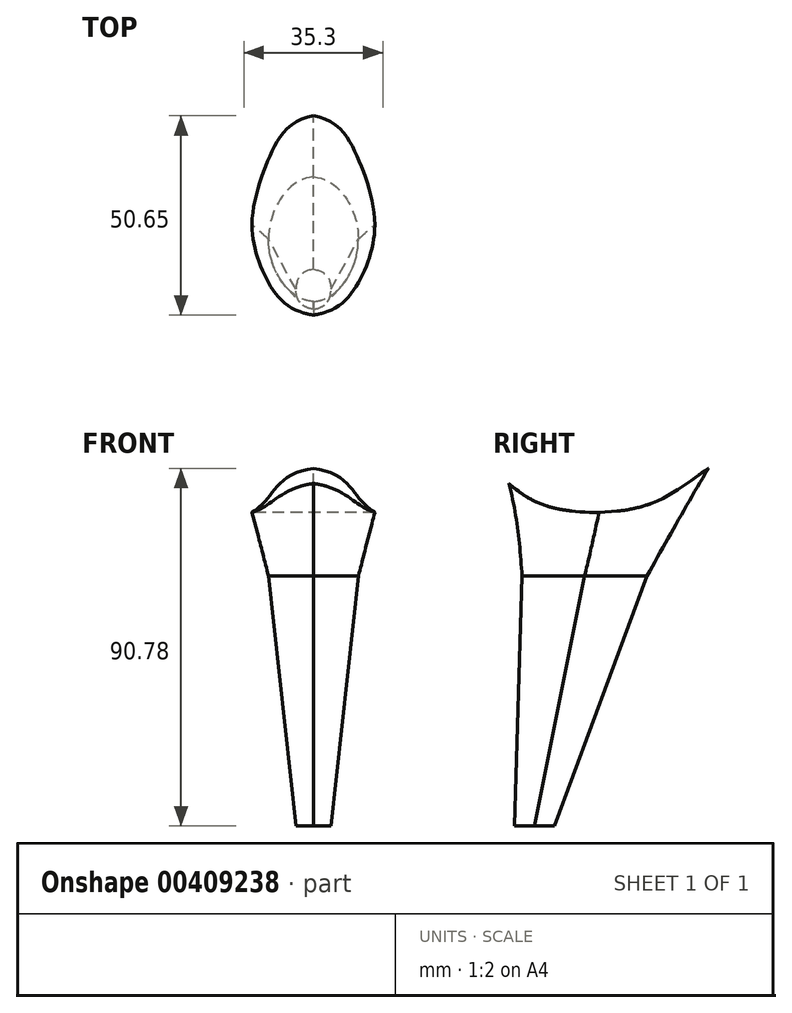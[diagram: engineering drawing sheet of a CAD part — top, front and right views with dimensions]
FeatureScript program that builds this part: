
annotation { "Feature Type Name" : "Feature", "Feature Type Description" : "" }
export const myFeature = defineFeature(function(context is Context, id is Id, definition is map)
    precondition{}
    {
        {
            var Q0;
            Q0=qCreatedBy(makeId("Top.planeOp"),FACE);
            var sketch = newSketch(context, id + "F0", { "sketchPlane" : qUnion([Q0])});
            skCircle(sketch, "E0", {"center": v(0, 0) * mm, "radius": 4.45 * mm, "construction": true});
            skFitSpline(sketch, "E1", {"points": [v(0, 5.08) * mm, v(-3.16, 3.63) * mm, v(-4.45, 0) * mm], "startDerivative": vector(-10.05, -1.39) * mm, "endDerivative": vector(-0.35, -12.15) * mm});
            skCircle(sketch, "E2", {"center": v(0, 0) * mm, "radius": 5.08 * mm, "construction": true});
            skFitSpline(sketch, "E3.MirrorCS", {"points": [v(0, 5.08) * mm, v(3.16, 3.63) * mm, v(4.45, 0) * mm], "startDerivative": vector(10.05, -1.39) * mm, "endDerivative": vector(0.35, -12.15) * mm});
            skFitSpline(sketch, "E4.MirrorCS", {"points": [v(0, 5.08) * mm, v(3.16, 3.63) * mm, v(4.45, 0) * mm], "startDerivative": vector(10.05, -1.39) * mm, "endDerivative": vector(0.35, -12.15) * mm});
            skFitSpline(sketch, "E5.MirrorCS", {"points": [v(0, -5.08) * mm, v(-3.16, -3.63) * mm, v(-4.45, 0) * mm], "startDerivative": vector(-10.05, 1.39) * mm, "endDerivative": vector(-0.35, 12.15) * mm});
            skFitSpline(sketch, "E6.MirrorCS", {"points": [v(0, -5.08) * mm, v(3.16, -3.63) * mm, v(4.45, 0) * mm], "startDerivative": vector(10.05, 1.39) * mm, "endDerivative": vector(0.35, 12.15) * mm});
            skSolve(sketch);
        }
        {
            var Q0;
            Q0=qCreatedBy(makeId("Top.planeOp"),FACE);
            cPlane(context, id + "F1", {"entities" : qUnion([Q0]), "cplaneType" : CPlaneType.OFFSET, "offset" : 63.5 * mm, "width" : 152.4 * mm, "height" : 152.4 * mm});
        }
        {
            var Q0;
            Q0=qCreatedBy(id+"F1.planeOp",FACE);
            var sketch = newSketch(context, id + "F2", { "sketchPlane" : qUnion([Q0])});
            skCircle(sketch, "E7", {"center": v(0, 12.7) * mm, "radius": 11.43 * mm, "construction": true});
            skCircle(sketch, "E8", {"center": v(0, 12.7) * mm, "radius": 15.88 * mm, "construction": true});
            skFitSpline(sketch, "E9", {"points": [v(0, 28.57) * mm, v(-7.97, 23.55) * mm, v(-11.43, 12.7) * mm], "startDerivative": vector(-23.5, -2.8) * mm, "endDerivative": vector(-0.5, -26.09) * mm});
            skFitSpline(sketch, "E10.MirrorCS", {"points": [v(0, 28.57) * mm, v(7.97, 23.55) * mm, v(11.43, 12.7) * mm], "startDerivative": vector(23.5, -2.8) * mm, "endDerivative": vector(0.5, -26.09) * mm});
            skLineSegment(sketch, "E11", {"start": v(-11.43, 12.7) * mm, "end": v(11.43, 12.7) * mm, "construction": true});
            skFitSpline(sketch, "E12.MirrorCS", {"points": [v(0, -3.17) * mm, v(-7.97, 1.85) * mm, v(-11.43, 12.7) * mm], "startDerivative": vector(-23.5, 2.8) * mm, "endDerivative": vector(-0.5, 26.09) * mm});
            skFitSpline(sketch, "E13.MirrorCS", {"points": [v(0, -3.17) * mm, v(7.97, 1.85) * mm, v(11.43, 12.7) * mm], "startDerivative": vector(23.5, 2.8) * mm, "endDerivative": vector(0.5, 26.09) * mm});
            skPoint(sketch, "E14.0", {"position": v(0, 0) * mm});
            skSolve(sketch);
        }
        {
            var Q0;
            Q0=makeQuery(id+"F0.imprint","IMPRINT",FACE,{"disambiguationData":[TD([[makeQuery(id+"F0.imprint","IMPRINT",EDGE,{"derivedFrom":sQuery(id+"F0.wireOp",EDGE,"E1")}),1.0]])]});
            var Q1;
            Q1=makeQuery(id+"F2.imprint","IMPRINT",FACE,{"disambiguationData":[TD([[makeQuery(id+"F2.imprint","IMPRINT",EDGE,{"derivedFrom":sQuery(id+"F2.wireOp",EDGE,"E9")}),1.0]])]});
            loft(context, id + "F3", {"sheetProfilesArray" : [{ "sheetProfileEntities" : qUnion([Q0]) }, { "sheetProfileEntities" : qUnion([Q1]) }]});
        }
        {
            var Q0;
            Q0=qCreatedBy(id+"F1.planeOp",FACE);
            cPlane(context, id + "F4", {"entities" : qUnion([Q0]), "cplaneType" : CPlaneType.OFFSET, "offset" : 38.1 * mm, "width" : 152.4 * mm, "height" : 152.4 * mm});
        }
        {
            var Q0;
            Q0=qCreatedBy(id+"F4.planeOp",FACE);
            var sketch = newSketch(context, id + "F5", { "sketchPlane" : qUnion([Q0])});
            skPoint(sketch, "E15.0", {"position": v(0, 0) * mm});
            skCircle(sketch, "E16", {"center": v(0, 19.05) * mm, "radius": 22.23 * mm, "construction": true});
            skCircle(sketch, "E17", {"center": v(0, 19.05) * mm, "radius": 31.75 * mm, "construction": true});
            skFitSpline(sketch, "E18", {"points": [v(0, 50.8) * mm, v(-14.15, 42.4) * mm, v(-22.22, 19.05) * mm], "startDerivative": vector(-46.14, -5.08) * mm, "endDerivative": vector(-0.3, -42.83) * mm});
            skLineSegment(sketch, "E19", {"start": v(-22.22, 19.05) * mm, "end": v(22.22, 19.05) * mm, "construction": true});
            skFitSpline(sketch, "E20.MirrorCS", {"points": [v(0, 50.8) * mm, v(14.15, 42.4) * mm, v(22.22, 19.05) * mm], "startDerivative": vector(46.14, -5.08) * mm, "endDerivative": vector(0.3, -42.83) * mm});
            skLineSegment(sketch, "E21.MirrorCS", {"start": v(22.22, 19.05) * mm, "end": v(-22.22, 19.05) * mm, "construction": true});
            skFitSpline(sketch, "E22.MirrorCS", {"points": [v(0, -12.7) * mm, v(-14.15, -4.3) * mm, v(-22.22, 19.05) * mm], "startDerivative": vector(-46.14, 5.08) * mm, "endDerivative": vector(-0.3, 42.83) * mm});
            skFitSpline(sketch, "E23.MirrorCS", {"points": [v(0, -12.7) * mm, v(14.15, -4.3) * mm, v(22.22, 19.05) * mm], "startDerivative": vector(46.14, 5.08) * mm, "endDerivative": vector(0.3, 42.83) * mm});
            skSolve(sketch);
        }
        {
            var Q0;
            Q0=qCreatedBy(id+"F4.planeOp",FACE);
            cPlane(context, id + "F6", {"entities" : qUnion([Q0]), "cplaneType" : CPlaneType.OFFSET, "offset" : 50.8 * mm, "width" : 152.4 * mm, "height" : 152.4 * mm});
        }
        {
            var Q0;
            Q0=qCreatedBy(id+"F6.planeOp",FACE);
            var sketch = newSketch(context, id + "F7", { "sketchPlane" : qUnion([Q0])});
            skPoint(sketch, "E24.0", {"position": v(0, 0) * mm});
            skCircle(sketch, "E25", {"center": v(0, 8.9) * mm, "radius": 44.45 * mm, "construction": true});
            skCircle(sketch, "E26", {"center": v(0, 8.9) * mm, "radius": 79.38 * mm, "construction": true});
            skFitSpline(sketch, "E27", {"points": [v(0, 88.26) * mm, v(-27.3, 62.72) * mm, v(-44.45, 8.9) * mm], "startDerivative": vector(-70.11, -4.65) * mm, "endDerivative": vector(4.08, -70.7) * mm});
            skLineSegment(sketch, "E28", {"start": v(-44.45, 8.9) * mm, "end": v(44.45, 8.9) * mm, "construction": true});
            skFitSpline(sketch, "E29.MirrorCS", {"points": [v(0, 88.26) * mm, v(27.3, 62.72) * mm, v(44.45, 8.9) * mm], "startDerivative": vector(70.11, -4.65) * mm, "endDerivative": vector(-4.08, -70.7) * mm});
            skFitSpline(sketch, "E30.MirrorCS", {"points": [v(0, -70.48) * mm, v(27.3, -44.94) * mm, v(44.45, 8.9) * mm], "startDerivative": vector(70.11, 4.65) * mm, "endDerivative": vector(-4.08, 70.7) * mm});
            skFitSpline(sketch, "E31.MirrorCS", {"points": [v(0, -70.48) * mm, v(-27.3, -44.94) * mm, v(-44.45, 8.9) * mm], "startDerivative": vector(-70.11, 4.65) * mm, "endDerivative": vector(4.08, 70.7) * mm});
            skSolve(sketch);
        }
        {
            var Q1;
            Q1=makeQuery(id+"F3.opLoft","CAP_FACE",FACE,{"disambiguationData":[OSD([makeQuery(id+"F2.imprint","IMPRINT",FACE,{"disambiguationData":[TD([[makeQuery(id+"F2.imprint","IMPRINT",EDGE,{"derivedFrom":sQuery(id+"F2.wireOp",EDGE,"E9")}),1.0]])]})])],"isStart":true});
            var Q2;
            Q2=makeQuery(id+"F5.imprint","IMPRINT",FACE,{"disambiguationData":[TD([[makeQuery(id+"F5.imprint","IMPRINT",EDGE,{"derivedFrom":sQuery(id+"F5.wireOp",EDGE,"E18")}),1.0]])]});
            var Q3;
            Q3=makeQuery(id+"F7.imprint","IMPRINT",FACE,{"disambiguationData":[TD([[makeQuery(id+"F7.imprint","IMPRINT",EDGE,{"derivedFrom":sQuery(id+"F7.wireOp",EDGE,"E27")}),1.0]])]});
            loft(context, id + "F8", {"sheetProfilesArray" : [{ "sheetProfileEntities" : qUnion([Q1]) }, { "sheetProfileEntities" : qUnion([Q2]) }, { "sheetProfileEntities" : qUnion([Q3]) }]});
        }
        {
            var Q0;
            Q0=qCreatedBy(makeId("Right.planeOp"),FACE);
            var sketch = newSketch(context, id + "F9", { "sketchPlane" : qUnion([Q0])});
            skFitSpline(sketch, "E32.0", {"points": [v(88.26, 152.4) * mm, v(77.06, 142.5) * mm, v(62.52, 131.17) * mm, v(37.92, 111.87) * mm, v(0.7, 109.17) * mm, v(-18.8, 117.07) * mm, v(-33.09, 124.93) * mm], "construction": true});
            skFitSpline(sketch, "E33.0", {"points": [v(-12.7, 101.6) * mm, v(-22.27, 119.4) * mm, v(-46.38, 135.9) * mm, v(-70.48, 152.4) * mm], "construction": true});
            skFitSpline(sketch, "E34.0", {"points": [v(50.8, 101.6) * mm, v(61.34, 119.4) * mm, v(74.8, 135.9) * mm, v(88.26, 152.4) * mm], "construction": true});
            skLineSegment(sketch, "E35", {"start": v(156.16, 101.92) * mm, "end": v(156.16, 185.2) * mm});
            skLineSegment(sketch, "E36", {"start": v(156.16, 185.2) * mm, "end": v(-81.97, 185.2) * mm});
            skLineSegment(sketch, "E37", {"start": v(-81.97, 185.2) * mm, "end": v(-81.97, 101.9) * mm});
            skFitSpline(sketch, "E38.0", {"points": [v(-6.74, 63.5) * mm, v(-6.42, 76.4) * mm, v(-6.1, 89.31) * mm, v(-12.7, 101.6) * mm]});
            skFitSpline(sketch, "E39.0", {"points": [v(31.75, 63.5) * mm, v(37.64, 76.4) * mm, v(43.52, 89.31) * mm, v(50.8, 101.6) * mm]});
            skFitSpline(sketch, "E40.0.0", {"points": [v(31.75, 63.5) * mm, v(37.64, 76.4) * mm, v(43.52, 89.31) * mm, v(50.8, 101.6) * mm], "construction": true});
            skFitSpline(sketch, "E40.0.1", {"points": [v(50.8, 101.6) * mm, v(61.34, 119.4) * mm, v(74.8, 135.9) * mm, v(88.26, 152.4) * mm], "construction": true});
            skFitSpline(sketch, "E40.0.2", {"points": [v(88.26, 152.4) * mm, v(61.8, 152.4) * mm, v(35.35, 152.4) * mm, v(8.9, 152.4) * mm], "construction": true});
            skFitSpline(sketch, "E40.0.3", {"points": [v(8.89, 152.4) * mm, v(14.21, 135.9) * mm, v(19.54, 119.4) * mm, v(19.05, 101.6) * mm], "construction": true});
            skFitSpline(sketch, "E40.0.4", {"points": [v(19.05, 101.6) * mm, v(18.71, 89.31) * mm, v(15.6, 76.4) * mm, v(12.5, 63.5) * mm], "construction": true});
            skFitSpline(sketch, "E40.0.5", {"points": [v(12.5, 63.5) * mm, v(18.92, 63.5) * mm, v(25.33, 63.5) * mm, v(31.75, 63.5) * mm], "construction": true});
            skFitSpline(sketch, "E41.0.0", {"points": [v(12.5, 63.5) * mm, v(15.6, 76.4) * mm, v(18.71, 89.31) * mm, v(19.05, 101.6) * mm], "construction": true});
            skFitSpline(sketch, "E41.0.1", {"points": [v(19.05, 101.6) * mm, v(19.54, 119.4) * mm, v(14.21, 135.9) * mm, v(8.9, 152.4) * mm], "construction": true});
            skFitSpline(sketch, "E41.0.2", {"points": [v(8.9, 152.4) * mm, v(-17.57, 152.4) * mm, v(-44.03, 152.4) * mm, v(-70.48, 152.4) * mm], "construction": true});
            skFitSpline(sketch, "E41.0.3", {"points": [v(-70.48, 152.4) * mm, v(-46.38, 135.9) * mm, v(-22.27, 119.4) * mm, v(-12.7, 101.6) * mm], "construction": true});
            skFitSpline(sketch, "E41.0.4", {"points": [v(-12.7, 101.6) * mm, v(-6.1, 89.31) * mm, v(-6.42, 76.4) * mm, v(-6.74, 63.5) * mm], "construction": true});
            skFitSpline(sketch, "E41.0.5", {"points": [v(-6.74, 63.5) * mm, v(-0.33, 63.5) * mm, v(6.09, 63.5) * mm, v(12.5, 63.5) * mm], "construction": true});
            skFitSpline(sketch, "E42.0.0", {"points": [v(31.75, 63.5) * mm, v(37.64, 76.4) * mm, v(43.52, 89.31) * mm, v(50.8, 101.6) * mm], "construction": true});
            skFitSpline(sketch, "E42.0.1", {"points": [v(50.8, 101.6) * mm, v(61.34, 119.4) * mm, v(74.8, 135.9) * mm, v(88.26, 152.4) * mm], "construction": true});
            skFitSpline(sketch, "E42.0.2", {"points": [v(88.26, 152.4) * mm, v(61.8, 152.4) * mm, v(35.35, 152.4) * mm, v(8.9, 152.4) * mm], "construction": true});
            skFitSpline(sketch, "E42.0.3", {"points": [v(8.89, 152.4) * mm, v(14.21, 135.9) * mm, v(19.54, 119.4) * mm, v(19.05, 101.6) * mm], "construction": true});
            skFitSpline(sketch, "E42.0.4", {"points": [v(19.05, 101.6) * mm, v(18.71, 89.31) * mm, v(15.6, 76.4) * mm, v(12.5, 63.5) * mm], "construction": true});
            skFitSpline(sketch, "E42.0.5", {"points": [v(12.5, 63.5) * mm, v(18.92, 63.5) * mm, v(25.33, 63.5) * mm, v(31.75, 63.5) * mm], "construction": true});
            skFitSpline(sketch, "E43.0.0", {"points": [v(31.75, 63.5) * mm, v(37.64, 76.4) * mm, v(43.52, 89.31) * mm, v(50.8, 101.6) * mm], "construction": true});
            skFitSpline(sketch, "E43.0.1", {"points": [v(50.8, 101.6) * mm, v(61.34, 119.4) * mm, v(74.8, 135.9) * mm, v(88.26, 152.4) * mm], "construction": true});
            skFitSpline(sketch, "E43.0.2", {"points": [v(88.26, 152.4) * mm, v(61.8, 152.4) * mm, v(35.35, 152.4) * mm, v(8.9, 152.4) * mm], "construction": true});
            skFitSpline(sketch, "E43.0.3", {"points": [v(8.89, 152.4) * mm, v(14.21, 135.9) * mm, v(19.54, 119.4) * mm, v(19.05, 101.6) * mm], "construction": true});
            skFitSpline(sketch, "E43.0.4", {"points": [v(19.05, 101.6) * mm, v(18.71, 89.31) * mm, v(15.6, 76.4) * mm, v(12.5, 63.5) * mm], "construction": true});
            skFitSpline(sketch, "E43.0.5", {"points": [v(12.5, 63.5) * mm, v(18.92, 63.5) * mm, v(25.33, 63.5) * mm, v(31.75, 63.5) * mm], "construction": true});
            skFitSpline(sketch, "E44", {"points": [v(-6.56, 86.98) * mm, v(8.49, 80.1) * mm, v(29.05, 81.7) * mm, v(44.1, 90.78) * mm], "startDerivative": vector(47.12, -42.16) * mm, "endDerivative": vector(45.96, 30.7) * mm});
            skLineSegment(sketch, "E45", {"start": v(44.1, 90.78) * mm, "end": v(156.16, 101.92) * mm});
            skLineSegment(sketch, "E46", {"start": v(-6.56, 86.98) * mm, "end": v(-81.97, 101.9) * mm});
            skSolve(sketch);
        }
        {
            var Q0;
            Q0 = qSketchRegion(id + "F9", true);
            extrude(context, id + "F10", {"entities" : qUnion([Q0]), "operationType" : NewBodyOperationType.REMOVE, "oppositeDirection" : true, "depth" : 71.12 * mm, "hasSecondDirection" : true, "secondDirectionOppositeDirection" : false, "secondDirectionDepth" : 58.42 * mm});
        }
    });
